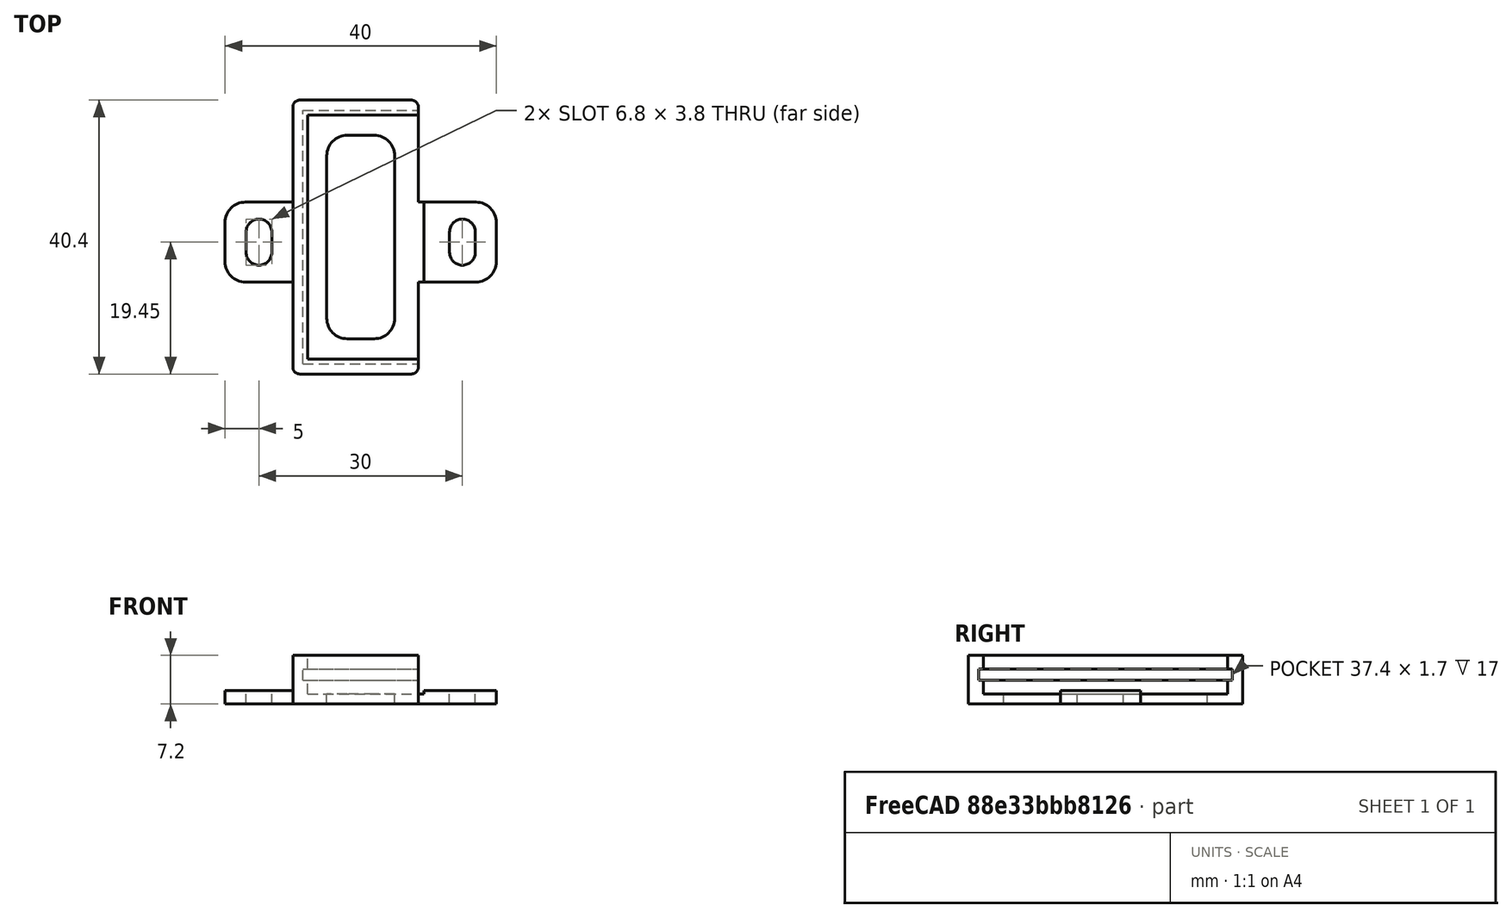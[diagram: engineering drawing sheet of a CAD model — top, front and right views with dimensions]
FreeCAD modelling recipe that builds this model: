
FCSTD DOCUMENT  (FreeCAD 0.19R23578 (Git))
Label: zs-040_bt4
License: FreeArt
LicenseURL: http://artlibre.org/licence/lal
objects: Part::Box×4, Part::Fillet×2, Part::MultiFuse×2, Spreadsheet::Sheet×1, Part::Feature×1, Part::Cut×1, App::Part×1
note: 10 computed .brp shape members not serialized (recipe doc carries the construction recipe); baked Part::Feature solids carry a one-line shape summary decoded from their .brp

FEATURE [Spreadsheet::Sheet] Spreadsheet  label="p"
  cells = A1=pcb_x; B1(pcb_x)=17; A2=pcb_y; B2(pcb_y)=37.4; A3=pcb_z; B3(pcb_z)=1.7; A4=pcb_under; B4(pcb_under)=2; A5=side_wall; B5(side_wall)=1.5; A6=pcb_side_lane; B6(pcb_side_lane)=0.7; A7=bottom_wall; B7(bottom_wall)=1.5; A8=pcb_above; B8(pcb_above)=2; A9=bottom_hole_x; B9(bottom_hole_x)=10; A10=bottom_hole_y; B10(bottom_hole_y)=30
FEATURE [Part::Box] Box  label="external cube"
  AttacherType = Attacher::AttachEngine3D
  Height = 7.2
  Length = 18.5
  Width = 40.4
  expr: Height = <<p>>.bottom_wall + <<p>>.pcb_under + <<p>>.pcb_z + <<p>>.pcb_above
  expr: Width = <<p>>.pcb_y + 2 * <<p>>.side_wall
  expr: Length = <<p>>.pcb_x + <<p>>.side_wall
FEATURE [Part::Box] Box006  label="internal cube"
  AttacherType = Attacher::AttachEngine3D
  Height = 5.7
  Length = 17.1
  Placement = pos=(2.2,2.2,1.5) rot=(0,0,1;0rad)
  Width = 36
  expr: .Placement.Base.y = <<p>>.side_wall + <<p>>.pcb_side_lane
  expr: .Placement.Base.x = <<p>>.side_wall + <<p>>.pcb_side_lane
  expr: .Placement.Base.z = <<p>>.bottom_wall
  expr: Height = <<p>>.pcb_under + <<p>>.pcb_z + <<p>>.pcb_above
  expr: Width = <<p>>.pcb_y - 2 * <<p>>.pcb_side_lane
  expr: Length = <<p>>.pcb_x - 2 * <<p>>.pcb_side_lane + <<p>>.side_wall
FEATURE [Part::Box] Box007  label="pcb extract cube"
  AttacherType = Attacher::AttachEngine3D
  Height = 1.7
  Length = 17
  Placement = pos=(1.5,1.5,3.5) rot=(0,0,1;0rad)
  Width = 37.4
  expr: .Placement.Base.y = <<p>>.side_wall
  expr: .Placement.Base.x = <<p>>.side_wall
  expr: Length = <<p>>.pcb_x
  expr: Width = <<p>>.pcb_y
  expr: .Placement.Base.z = <<p>>.bottom_wall + <<p>>.pcb_under
  expr: Height = <<p>>.pcb_z
FEATURE [Part::Fillet] Fillet  label="external fillet"
  Base = -> Box
  Edges = 4 edges r=1: [Edge1,Edge3,Edge5,Edge7]
FEATURE [Part::Box] Box008  label="bottom hole"
  AttacherType = Attacher::AttachEngine3D
  Height = 10
  Length = 10
  Placement = pos=(5,5.2,0) rot=(0,0,1;0rad)
  Width = 30
  expr: Length = <<p>>.bottom_hole_x
  expr: Width = <<p>>.bottom_hole_y
  expr: .Placement.Base.x = (<<p>>.pcb_x + 2 * <<p>>.side_wall - <<p>>.bottom_hole_x) / 2
  expr: .Placement.Base.y = (<<p>>.pcb_y + 2 * <<p>>.side_wall - <<p>>.bottom_hole_y) / 2
FEATURE [Part::Fillet] Fillet001  label="bottom hole fillet"
  Base = -> Box008
  Edges = 4 edges r=3: [Edge1,Edge3,Edge5,Edge7]
FEATURE [Part::MultiFuse] Fusion  label="extract fusion"
  Shapes = -> [Box006,Box007,Fillet001]
FEATURE [Part::Feature] Cut003001  label="attach plane x dir001"
  Placement = pos=(-10,13.55,0) rot=(0,0,1;0rad)
  shape: bbox 40 x 11.8 x 2 mm, 18 faces (baked)
FEATURE [Part::MultiFuse] Fusion001  label="solid fusion"
  Shapes = -> [Fillet,Cut003001]
FEATURE [Part::Cut] Cut  label="body cut"
  Base = -> Fusion001
  Tool = -> Fusion
FEATURE [App::Part] Part  label="pcb box part"
  Group = -> [Box,Fillet,Fusion001,Fusion,Box007,Box006,Cut]
  Origin = -> Origin
